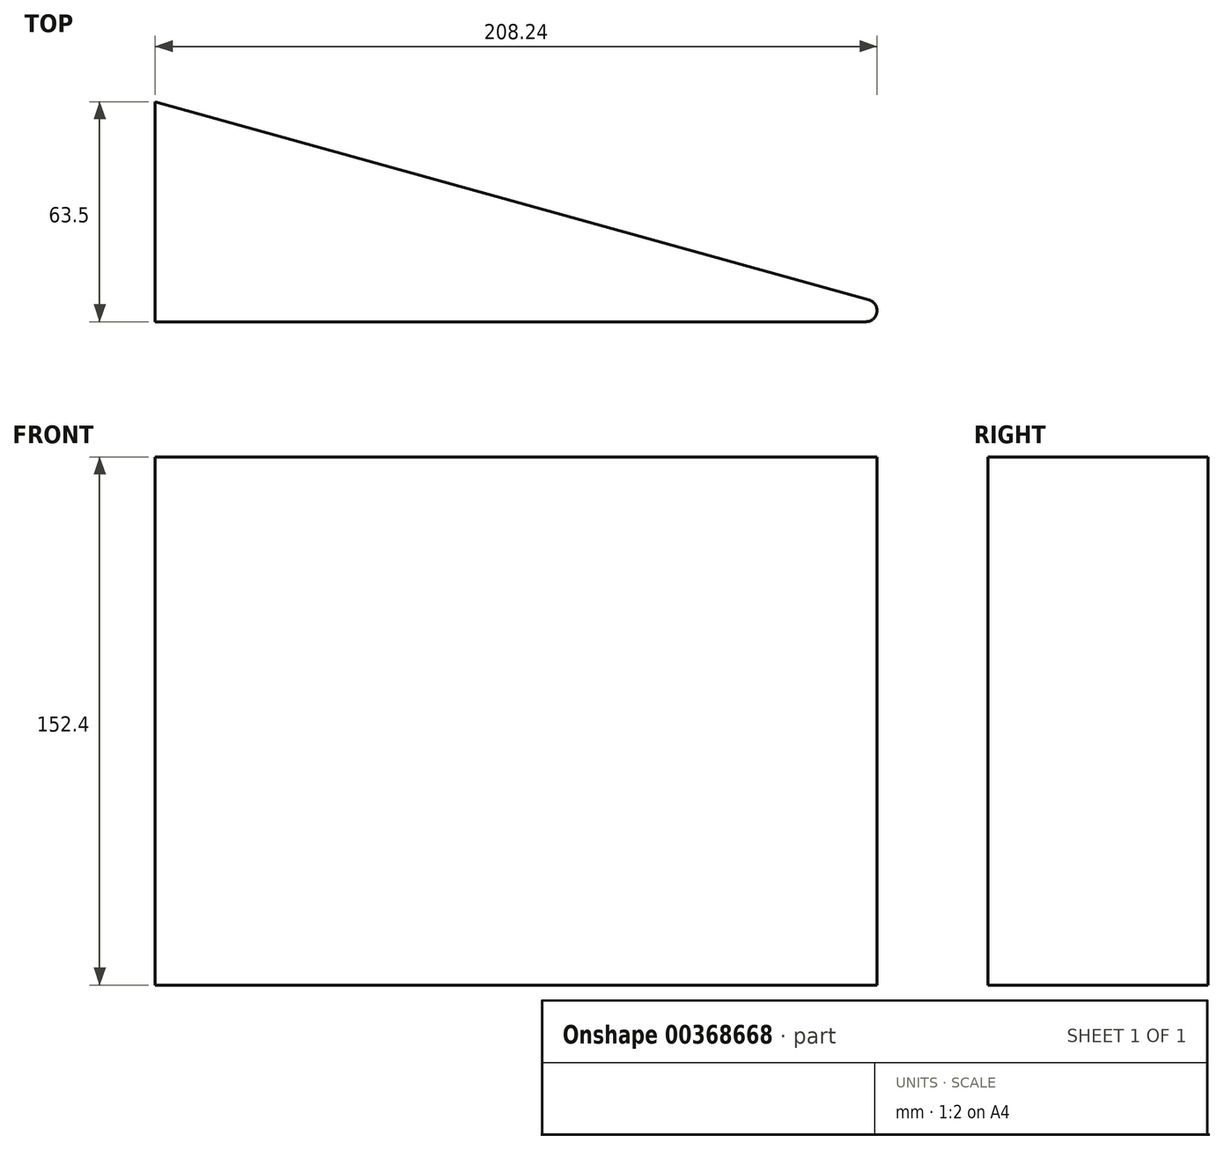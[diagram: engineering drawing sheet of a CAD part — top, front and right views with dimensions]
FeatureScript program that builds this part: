
annotation { "Feature Type Name" : "Feature", "Feature Type Description" : "" }
export const myFeature = defineFeature(function(context is Context, id is Id, definition is map)
    precondition{}
    {
        {
            var Q0;
            Q0=qCreatedBy(makeId("Top.planeOp"),FACE);
            var sketch = newSketch(context, id + "F0", { "sketchPlane" : qUnion([Q0])});
            skLineSegment(sketch, "E0", {"start": v(0, 0) * mm, "end": v(0, 63.5) * mm});
            skLineSegment(sketch, "E1", {"start": v(0, 0) * mm, "end": v(228.6, 0) * mm});
            skLineSegment(sketch, "E2", {"start": v(228.6, 0) * mm, "end": v(0, 63.5) * mm});
            skSolve(sketch);
        }
        {
            var Q0;
            Q0=makeQuery(id+"F0.imprint","IMPRINT",FACE,{"disambiguationData":[TD([[makeQuery(id+"F0.imprint","IMPRINT",EDGE,{"derivedFrom":sQuery(id+"F0.wireOp",EDGE,"E0")}),-1.0]])]});
            extrude(context, id + "F1", {"entities" : qUnion([Q0]), "depth" : 152.4 * mm});
        }
        {
            var Q0;
            Q0=makeQuery(id+"F1.opExtrude","SWEPT_EDGE",EDGE,{"disambiguationData":[OSD([sQuery(id+"F0.wireOp",EDGE,"E1"),sQuery(id+"F0.wireOp",EDGE,"E2")])]});
            fillet(context, id + "F2", {"entities" : qUnion([Q0]), "radius" : 3.2 * mm, "tangentPropagation" : true, "allowEdgeOverflow" : false});
        }
    });
